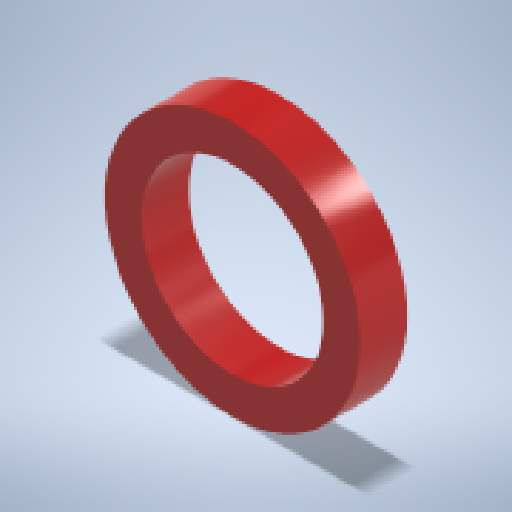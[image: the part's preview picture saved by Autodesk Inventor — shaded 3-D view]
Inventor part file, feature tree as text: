
AUTODESK INVENTOR PART (.ipt)
format: ipt  version: 2024 (Build 280153000, 153)  size: 252,416 bytes
history: native  units: mm
features: extrude x1, direct_edit x1, sketch x1, move_body x1
ambient origin geometry x8: Origin, YZ Plane, XZ Plane, XY Plane, X Axis, Y Axis, Z Axis, Center Point
bodies: Solid1 (feature_tree)
feature tree (4):
  extrude  "Extrusion1"  Depth=27.0mm
  direct_edit  "Direct Edit1"
  sketch  "Sketch1"  dims[d0=38.0mm d1=27.0mm d2=5.0mm d3=0.0mm d4=0.0mm d5=0.0mm d6=2.0mm]
  move_body  "Move1"
